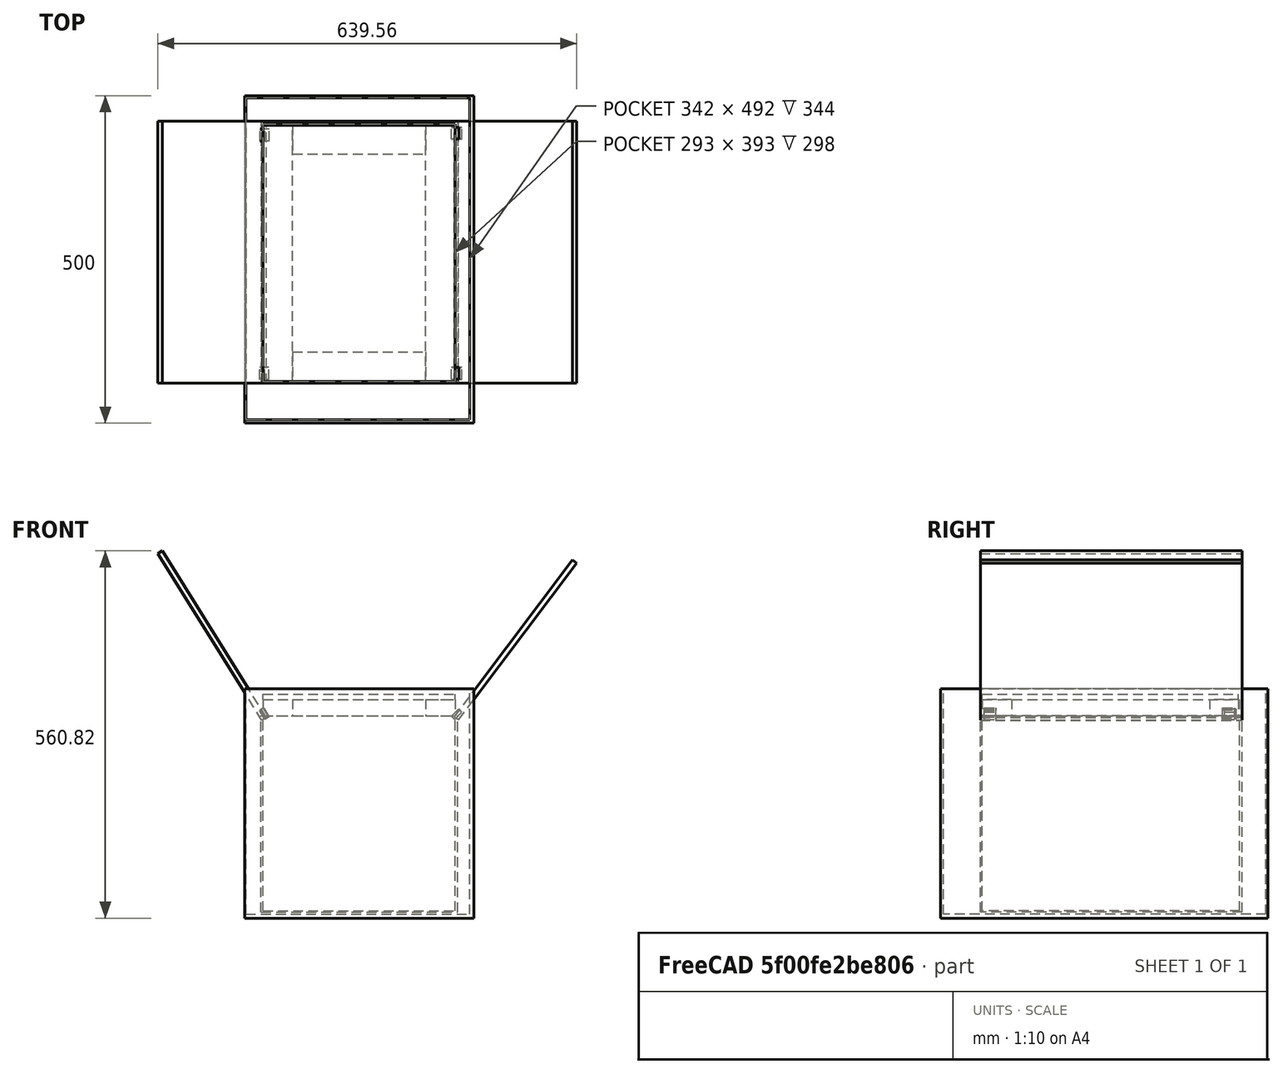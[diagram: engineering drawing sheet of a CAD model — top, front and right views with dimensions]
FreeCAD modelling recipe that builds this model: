
FCSTD DOCUMENT  (FreeCAD 0.21R33771 (Git))
Label: Grupo 6 Horno Solar 3D ABP2)(1)
License: All rights reserved
LicenseURL: https://en.wikipedia.org/wiki/All_rights_reserved
objects: Part::Box×15, Part::Cut×2
note: 17 computed .brp shape members not serialized (recipe doc carries the construction recipe); baked Part::Feature solids carry a one-line shape summary decoded from their .brp

FEATURE [Part::Box] Box007  label="Cubo007"
  AttacherType = Attacher::AttachEngine3D
  Height = 350
  Length = 500
  Placement = pos=(0,-360,593) rot=(0,0,1;0rad)
  Width = 350
FEATURE [Part::Box] Box008  label="Cubo008"
  AttacherType = Attacher::AttachEngine3D
  Height = 350
  Length = 492
  Placement = pos=(3,-358,599) rot=(0,0,1;0rad)
  Width = 342
FEATURE [Part::Cut] Cut001  label="Cajaota"
  Base = -> Box007
  Placement = pos=(375.7,556,-546) rot=(0,0,-1;1.5708rad)
  Tool = -> Box008
FEATURE [Part::Box] Box010  label="espejo1"
  AttacherType = Attacher::AttachEngine3D
  Height = 8
  Length = 300
  Placement = pos=(48.98,117,353.41) rot=(0,1,0;4.15388rad)
  Width = 400
FEATURE [Part::Box] Box012  label="CRistal"
  AttacherType = Attacher::AttachEngine3D
  Height = 8
  Length = 293
  Placement = pos=(44,120,381) rot=(0,0,1;0rad)
  Width = 391
FEATURE [Part::Box] Box011  label="espejo002"
  AttacherType = Attacher::AttachEngine3D
  Height = 8
  Length = 300
  Placement = pos=(342.238,117,349.565) rot=(0,-1,0;0.925025rad)
  Width = 400
FEATURE [Part::Box] Box017  label="bisagra001"
  AttacherType = Attacher::AttachEngine3D
  Height = 16
  Length = 18
  Placement = pos=(336.381,123,350.588) rot=(0.357407,0.357407,0.862856;1.71777rad)
  Width = 7
FEATURE [Part::Box] Box018  label="bisagra002"
  AttacherType = Attacher::AttachEngine3D
  Height = 16
  Length = 18
  Placement = pos=(336.381,490,350.588) rot=(0.357407,0.357407,0.862856;1.71777rad)
  Width = 7
FEATURE [Part::Box] Box019  label="bisagra003"
  AttacherType = Attacher::AttachEngine3D
  Height = 16
  Length = 18
  Placement = pos=(53.3608,487.011,354.483) rot=(-0.248932,-0.248932,0.935984;1.63782rad)
  Width = 7
FEATURE [Part::Box] Box020  label="bisagra004"
  AttacherType = Attacher::AttachEngine3D
  Height = 16
  Length = 18
  Placement = pos=(52.6186,123,354.054) rot=(-0.250563,-0.250563,0.935113;1.63783rad)
  Width = 7
FEATURE [Part::Box] Box021  label="Palo Primero"
  AttacherType = Attacher::AttachEngine3D
  Height = 391
  Length = 45
  Placement = pos=(44,120,381) rot=(-1,0,0;1.5708rad)
  Width = 25
FEATURE [Part::Box] Box022  label="Palo Segundo"
  AttacherType = Attacher::AttachEngine3D
  Height = 392
  Length = 45
  Placement = pos=(292,120,381) rot=(-1,0,0;1.5708rad)
  Width = 25
FEATURE [Part::Box] Box023  label="Palo Tercero (corto)"
  AttacherType = Attacher::AttachEngine3D
  Height = 203
  Length = 45
  Placement = pos=(89,512,381) rot=(0.57735,-0.57735,0.57735;4.18879rad)
  Width = 25
FEATURE [Part::Box] Box024  label="Palo Cuarto (cCOrto)"
  AttacherType = Attacher::AttachEngine3D
  Height = 203
  Length = 45
  Placement = pos=(89,165,381) rot=(0.57735,-0.57735,0.57735;4.18879rad)
  Width = 25
FEATURE [Part::Box] Box  label="Cubo"
  AttacherType = Attacher::AttachEngine3D
  Height = 300
  Length = 400
  Width = 300
FEATURE [Part::Box] Box025  label="Cubo009"
  AttacherType = Attacher::AttachEngine3D
  Height = 324
  Length = 393
  Placement = pos=(4,3,2) rot=(0,0,1;0rad)
  Width = 293
FEATURE [Part::Cut] Cut  label="cajita"
  Base = -> Box
  Placement = pos=(41,517,56) rot=(0,0,-1;1.5708rad)
  Tool = -> Box025
